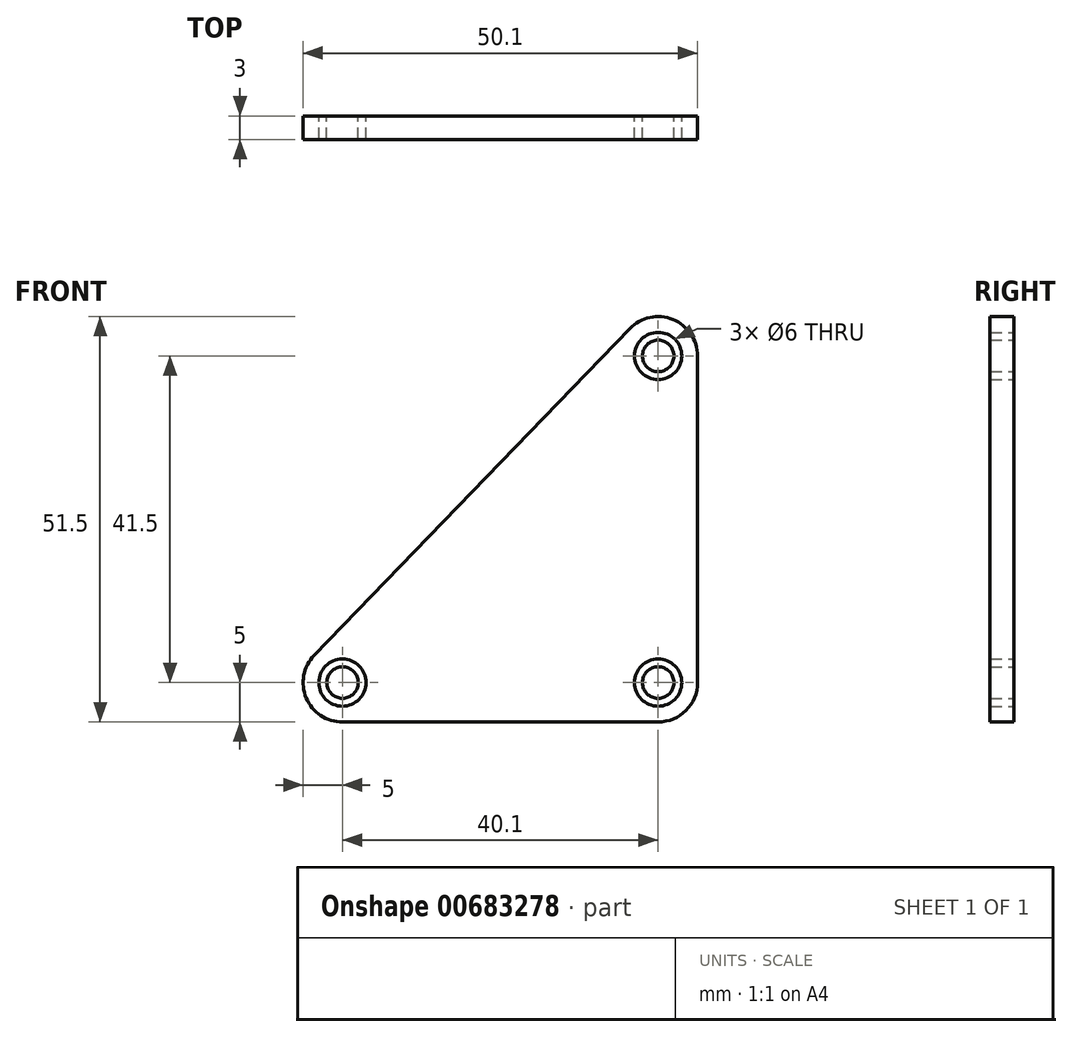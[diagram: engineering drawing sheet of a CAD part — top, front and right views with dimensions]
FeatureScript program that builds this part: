
annotation { "Feature Type Name" : "Feature", "Feature Type Description" : "" }
export const myFeature = defineFeature(function(context is Context, id is Id, definition is map)
    precondition{}
    {
        {
            var Q0;
            Q0=qCreatedBy(makeId("Front.planeOp"),FACE);
            var sketch = newSketch(context, id + "F0", { "sketchPlane" : qUnion([Q0])});
            skCircle(sketch, "E0", {"center": v(0, 41.5) * mm, "radius": 3 * mm});
            skCircle(sketch, "E1", {"center": v(0, 0) * mm, "radius": 3 * mm});
            skCircle(sketch, "E2", {"center": v(-40.1, 0) * mm, "radius": 3 * mm});
            skArc(sketch, "E3", {"start": v(-43.7, 3.47) * mm, "mid": v(-44.7, -1.95) * mm, "end": v(-40.1, -5) * mm});
            skArc(sketch, "E4", {"start": v(0, -5) * mm, "mid": v(3.54, -3.54) * mm, "end": v(5, 0) * mm});
            skArc(sketch, "E5", {"start": v(5, 41.5) * mm, "mid": v(1.87, 46.14) * mm, "end": v(-3.6, 44.97) * mm});
            skLineSegment(sketch, "E6", {"start": v(-43.7, 3.47) * mm, "end": v(-3.6, 44.97) * mm});
            skLineSegment(sketch, "E7", {"start": v(5, 41.5) * mm, "end": v(5, 0) * mm});
            skLineSegment(sketch, "E8", {"start": v(-40.1, -5) * mm, "end": v(0, -5) * mm});
            skCircle(sketch, "E9", {"center": v(-40.1, 0) * mm, "radius": 2 * mm});
            skCircle(sketch, "E10", {"center": v(0, 0) * mm, "radius": 2 * mm});
            skCircle(sketch, "E11", {"center": v(0, 41.5) * mm, "radius": 2 * mm});
            skSolve(sketch);
        }
        {
            var Q0;
            Q0 = qSketchRegion(id + "F0", true);
            var Q1;
            Q1=makeQuery(id+"F0.imprint","IMPRINT",FACE,{"disambiguationData":[TD([[makeQuery(id+"F0.imprint","IMPRINT",EDGE,{"derivedFrom":sQuery(id+"F0.wireOp",EDGE,"E9")}),1.0]])]});
            var Q2;
            Q2=makeQuery(id+"F0.imprint","IMPRINT",FACE,{"disambiguationData":[TD([[makeQuery(id+"F0.imprint","IMPRINT",EDGE,{"derivedFrom":sQuery(id+"F0.wireOp",EDGE,"E10")}),1.0]])]});
            var Q3;
            Q3=makeQuery(id+"F0.imprint","IMPRINT",FACE,{"disambiguationData":[TD([[makeQuery(id+"F0.imprint","IMPRINT",EDGE,{"derivedFrom":sQuery(id+"F0.wireOp",EDGE,"E11")}),1.0]])]});
            extrude(context, id + "F1", {"entities" : qUnion([Q0, Q1, Q2, Q3]), "depth" : 3 * mm, "offsetDistance" : 25 * mm});
        }
    });
